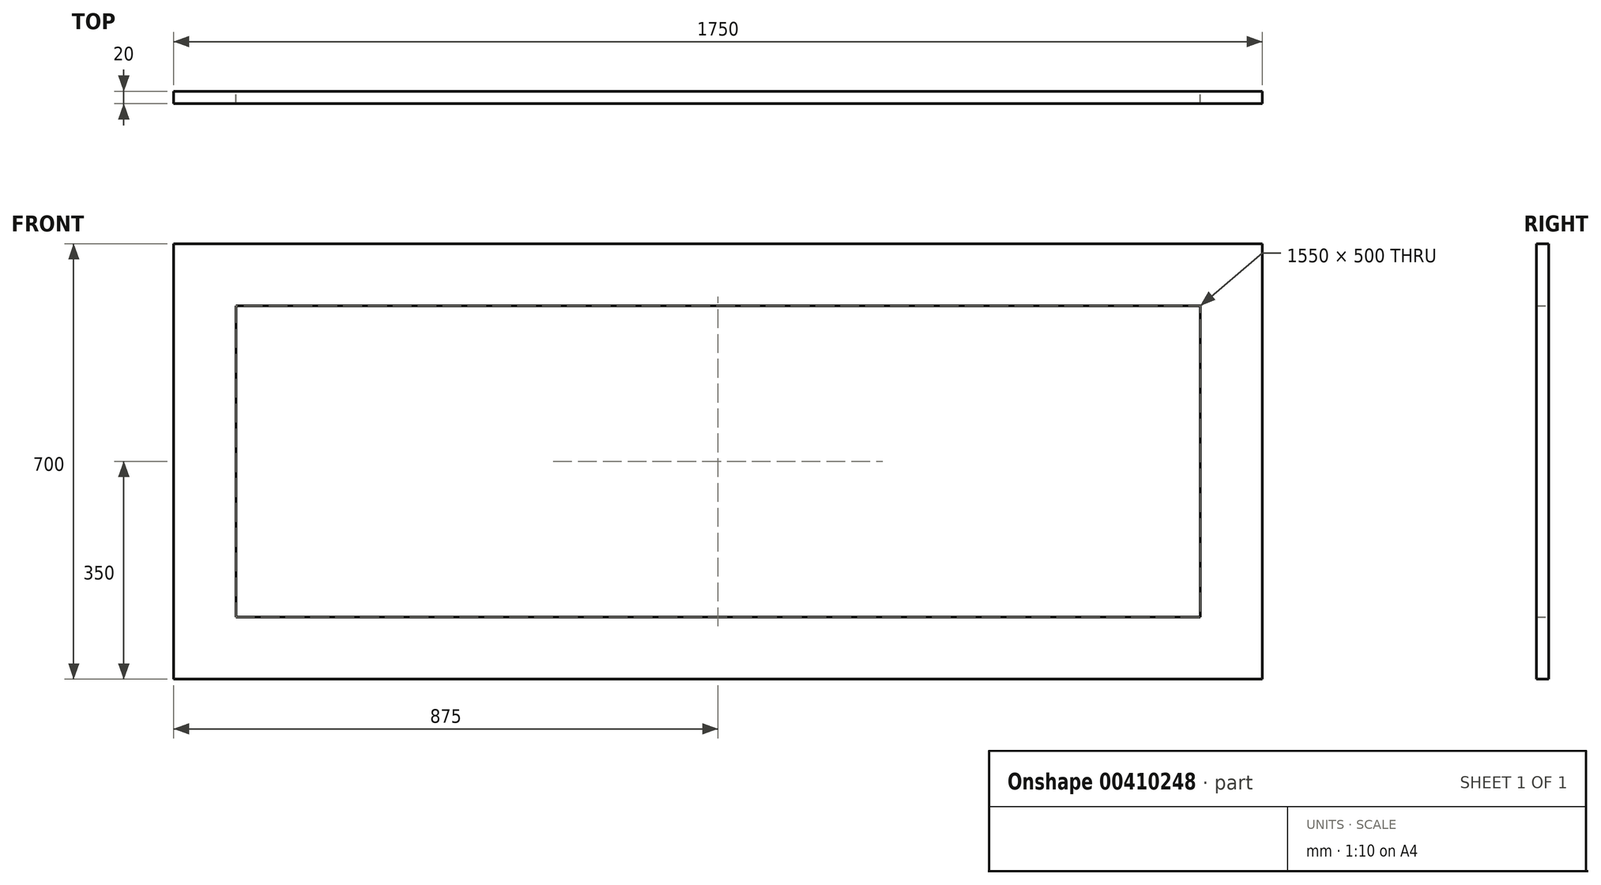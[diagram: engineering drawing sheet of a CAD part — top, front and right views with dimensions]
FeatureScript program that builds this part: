
annotation { "Feature Type Name" : "Feature", "Feature Type Description" : "" }
export const myFeature = defineFeature(function(context is Context, id is Id, definition is map)
    precondition{}
    {
        {
            var Q0;
            Q0=qCreatedBy(makeId("Front.planeOp"),FACE);
            var sketch = newSketch(context, id + "F0", { "sketchPlane" : qUnion([Q0])});
            skLineSegment(sketch, "E0.bottom", {"start": v(875, -350) * mm, "end": v(-875, -350) * mm});
            skLineSegment(sketch, "E0.top", {"start": v(875, 350) * mm, "end": v(-875, 350) * mm});
            skLineSegment(sketch, "E0.left", {"start": v(875, -350) * mm, "end": v(875, 350) * mm});
            skLineSegment(sketch, "E0.right", {"start": v(-875, -350) * mm, "end": v(-875, 350) * mm});
            skPoint(sketch, "E0.middle", {"position": v(0, 0) * mm});
            skLineSegment(sketch, "E1.0", {"start": v(775, 250) * mm, "end": v(-775, 250) * mm});
            skLineSegment(sketch, "E1.1", {"start": v(-775, -250) * mm, "end": v(-775, 250) * mm});
            skLineSegment(sketch, "E1.2", {"start": v(775, -250) * mm, "end": v(-775, -250) * mm});
            skLineSegment(sketch, "E1.3", {"start": v(775, -250) * mm, "end": v(775, 250) * mm});
            skSolve(sketch);
        }
        {
            var Q0;
            Q0 = qSketchRegion(id + "F0", true);
            extrude(context, id + "F1", {"entities" : qUnion([Q0]), "domain" : OperationDomain.MODEL, "flatOperationType" : FlatOperationType.REMOVE, "endBound" : BoundingType.SYMMETRIC, "depth" : 20 * mm, "offsetDistance" : 25 * mm});
        }
    });
